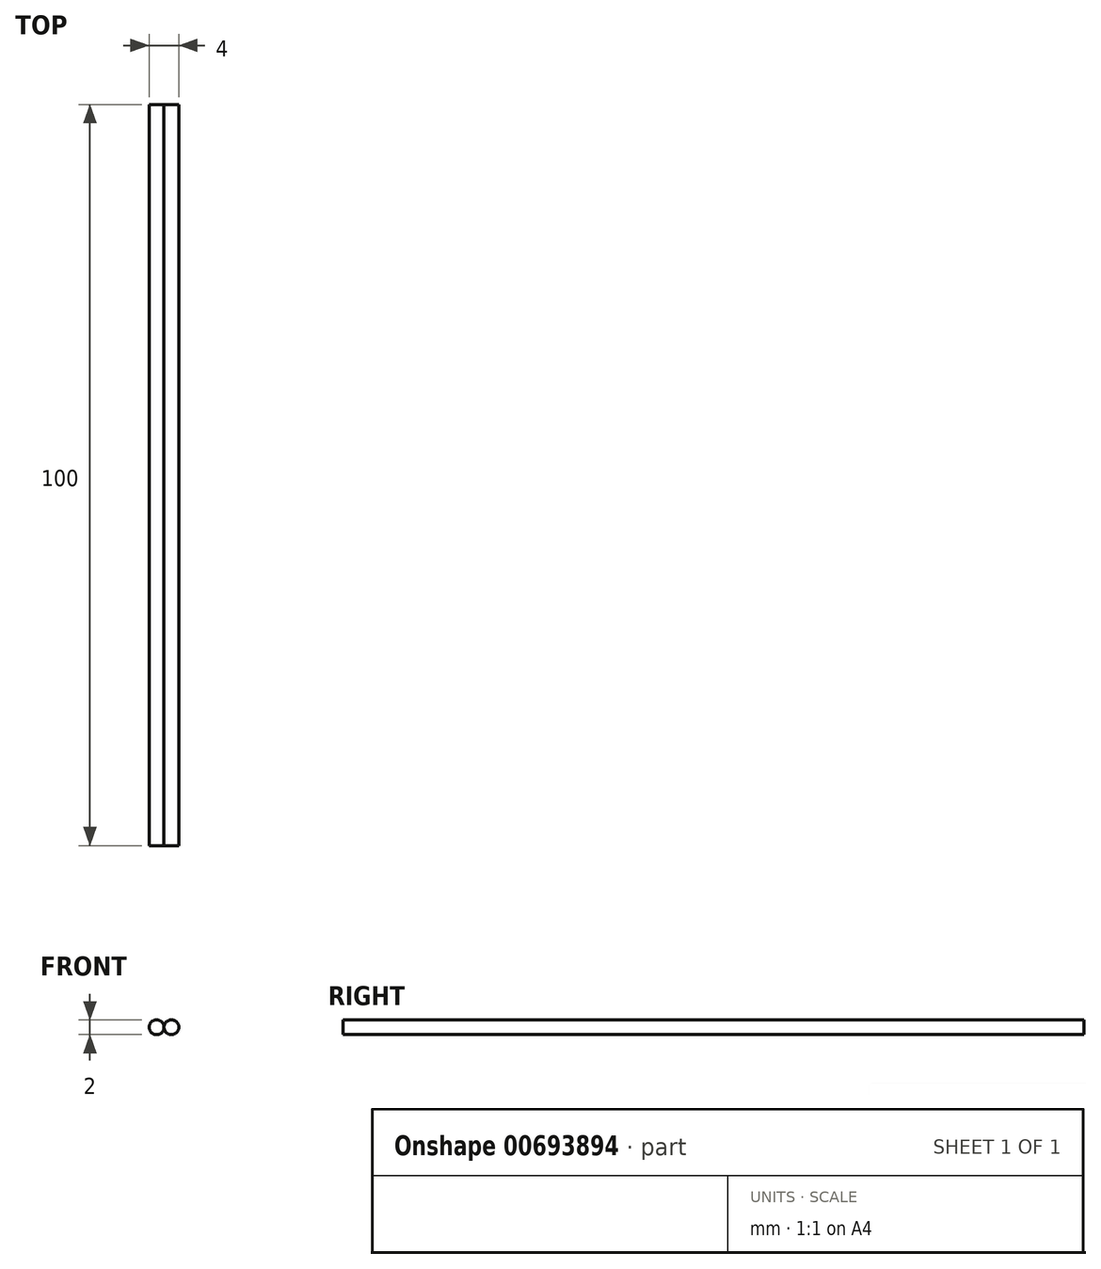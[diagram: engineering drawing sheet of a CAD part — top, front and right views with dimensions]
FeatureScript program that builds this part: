
annotation { "Feature Type Name" : "Feature", "Feature Type Description" : "" }
export const myFeature = defineFeature(function(context is Context, id is Id, definition is map)
    precondition{}
    {
        {
            var Q0;
            Q0=qCreatedBy(makeId("Front.planeOp"),FACE);
            var sketch = newSketch(context, id + "F0", { "sketchPlane" : qUnion([Q0])});
            skCircle(sketch, "E0", {"center": v(0, 0) * mm, "radius": 1 * mm});
            skCircle(sketch, "E1", {"center": v(2, 0) * mm, "radius": 1 * mm});
            skSolve(sketch);
        }
        {
            var Q0;
            Q0 = qSketchRegion(id + "F0", true);
            extrude(context, id + "F1", {"entities" : qUnion([Q0]), "oppositeDirection" : true, "depth" : 100 * mm, "offsetDistance" : 25.4 * mm});
        }
    });
